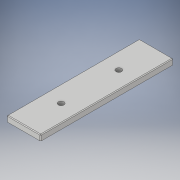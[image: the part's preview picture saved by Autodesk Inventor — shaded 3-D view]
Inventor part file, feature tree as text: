
AUTODESK INVENTOR PART (.ipt)
format: ipt  version: 2019.4 (Build 234330000, 330)  size: 112,128 bytes
history: native  units: in
note: dims shown in document units (in); Inventor stores cm internally (conversion verified against a paired STEP export)
features: sketch x2, extrude x1, hole x1, chamfer x1
ambient origin geometry x8: Origin, YZ Plane, XZ Plane, XY Plane, X Axis, Y Axis, Z Axis, Center Point
bodies: Solid1 (feature_tree)
feature tree (5):
  extrude  "Extrusion1"  Depth=1.5in
  hole  "Hole1"  [1 undecoded]
  chamfer  "Chamfer1"  Distance=1.2795in
  sketch  "Sketch1"  dims[d0=5.875in d1=1.5in]
  sketch  "Sketch2"  dims[d2=0.25in d3=0.0in d4=1.2795in d5=1.2795in d6=0.25in d7=0.157in d8=0.375in d9=0.25in d10=0.5635in d11=1.0in d12=0.8108in d13=0.0312in d14=0.125in d15=45.0deg]
note: 1 required parameter value undecoded (feature->parameter linkage not recoverable at this tier; creation-order binding heuristic only, values carry confidence <= 0.55)
